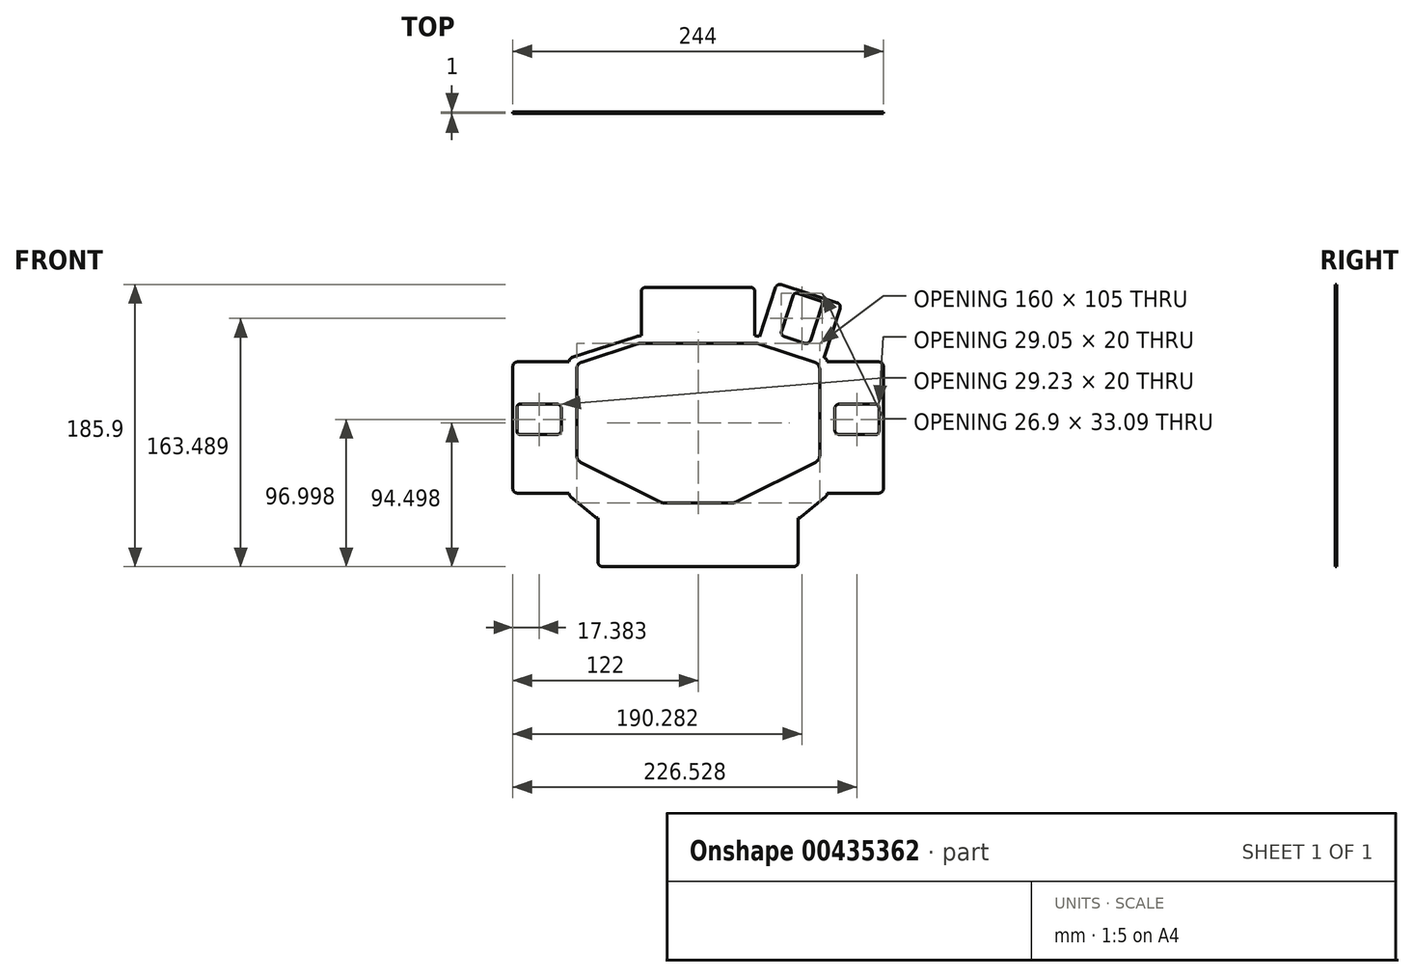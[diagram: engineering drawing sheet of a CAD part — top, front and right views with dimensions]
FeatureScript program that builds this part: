
annotation { "Feature Type Name" : "Feature", "Feature Type Description" : "" }
export const myFeature = defineFeature(function(context is Context, id is Id, definition is map)
    precondition{}
    {
        {
            var Q0;
            Q0=qCreatedBy(makeId("Front.planeOp"),FACE);
            var sketch = newSketch(context, id + "F0", { "sketchPlane" : qUnion([Q0])});
            skLineSegment(sketch, "E0", {"start": v(85, 6.93) * mm, "end": v(85, 93.35) * mm});
            skLineSegment(sketch, "E1", {"start": v(82.93, 96.2) * mm, "end": v(40.51, 110.04) * mm});
            skLineSegment(sketch, "E2", {"start": v(83.92, 4.63) * mm, "end": v(67.83, -8.78) * mm});
            skLineSegment(sketch, "E3", {"start": v(85, 95.53) * mm, "end": v(85, 25.53) * mm});
            skLineSegment(sketch, "E4", {"start": v(39.76, 105.28) * mm, "end": v(76.55, 93.28) * mm});
            skLineSegment(sketch, "E5", {"start": v(85, 90.53) * mm, "end": v(85, 95.53) * mm});
            skLineSegment(sketch, "E6", {"start": v(80, 88.53) * mm, "end": v(80, 31.7) * mm});
            skLineSegment(sketch, "E7", {"start": v(77.24, 27.24) * mm, "end": v(24.88, 1.06) * mm});
            skLineSegment(sketch, "E8", {"start": v(0, 0) * mm, "end": v(0, 0.53) * mm});
            skPoint(sketch, "E8.endSnap0", {"position": v(0, 0) * mm});
            skLineSegment(sketch, "E9", {"start": v(0, 0.53) * mm, "end": v(22.64, 0.53) * mm});
            skPoint(sketch, "E10.orphan", {"position": v(22.76, 0) * mm});
            skPoint(sketch, "E11.visualSharp", {"position": v(80, 92.16) * mm});
            skArc(sketch, "E11.filletArc", {"start": v(80, 88.53) * mm, "mid": v(79.05, 91.47) * mm, "end": v(76.55, 93.28) * mm});
            skPoint(sketch, "E12.visualSharp", {"position": v(80, 28.62) * mm});
            skArc(sketch, "E12.filletArc", {"start": v(77.24, 27.24) * mm, "mid": v(79.25, 29.08) * mm, "end": v(80, 31.7) * mm});
            skPoint(sketch, "E13.visualSharp", {"position": v(23.82, 0.53) * mm});
            skArc(sketch, "E13.filletArc", {"start": v(22.64, 0.53) * mm, "mid": v(23.79, 0.66) * mm, "end": v(24.88, 1.06) * mm});
            skPoint(sketch, "E14.visualSharp", {"position": v(39, 105.53) * mm});
            skArc(sketch, "E14.filletArc", {"start": v(39.76, 105.28) * mm, "mid": v(39, 105.47) * mm, "end": v(38.2, 105.53) * mm});
            skLineSegment(sketch, "E15", {"start": v(40.51, 110.04) * mm, "end": v(62, 103.03) * mm});
            skLineSegment(sketch, "E16", {"start": v(62, 103.03) * mm, "end": v(71.5, 99.93) * mm});
            skLineSegment(sketch, "E17", {"start": v(71.5, 99.93) * mm, "end": v(52.5, 106.13) * mm});
            skPoint(sketch, "E18.visualSharp", {"position": v(67, -9.47) * mm});
            skArc(sketch, "E18.filletArc", {"start": v(65.91, -9.47) * mm, "mid": v(66.94, -9.3) * mm, "end": v(67.83, -8.78) * mm});
            skPoint(sketch, "E19.visualSharp", {"position": v(85, 5.53) * mm});
            skArc(sketch, "E19.filletArc", {"start": v(83.92, 4.63) * mm, "mid": v(84.72, 5.66) * mm, "end": v(85, 6.93) * mm});
            skLineSegment(sketch, "E20", {"start": v(85, 95.53) * mm, "end": v(85, 65.53) * mm});
            skLineSegment(sketch, "E21", {"start": v(85, 65.53) * mm, "end": v(85, 45.53) * mm});
            skPoint(sketch, "E22.visualSharp", {"position": v(39, 110.53) * mm});
            skPoint(sketch, "E23.visualSharp", {"position": v(85, 95.53) * mm});
            skArc(sketch, "E23.filletArc", {"start": v(85, 93.35) * mm, "mid": v(84.43, 95.11) * mm, "end": v(82.93, 96.2) * mm});
            skLineSegment(sketch, "E24", {"start": v(85, 93.35) * mm, "end": v(114, 93.35) * mm});
            skLineSegment(sketch, "E25", {"start": v(85, 6.93) * mm, "end": v(114, 6.93) * mm});
            skPoint(sketch, "E26.visualSharp", {"position": v(117, 6.93) * mm});
            skPoint(sketch, "E27.newPointB", {"position": v(85, 45.53) * mm});
            skPoint(sketch, "E28.visualSharp", {"position": v(117, 93.35) * mm});
            skLineSegment(sketch, "E29", {"start": v(65.91, -9.47) * mm, "end": v(65.91, -38.47) * mm});
            skPoint(sketch, "E30.visualSharp", {"position": v(65.91, -41.47) * mm});
            skArc(sketch, "E30.filletArc", {"start": v(62.91, -41.47) * mm, "mid": v(65.04, -40.6) * mm, "end": v(65.91, -38.47) * mm});
            skArc(sketch, "E31.filletArc", {"start": v(40.51, 110.04) * mm, "mid": v(38.98, 110.4) * mm, "end": v(37.41, 110.53) * mm});
            skLineSegment(sketch, "E32", {"start": v(37.41, 110.53) * mm, "end": v(37.41, 139.53) * mm});
            skPoint(sketch, "E33.visualSharp", {"position": v(37.41, 142.53) * mm});
            skArc(sketch, "E33.filletArc", {"start": v(37.41, 139.53) * mm, "mid": v(36.53, 141.65) * mm, "end": v(34.41, 142.53) * mm});
            skLineSegment(sketch, "E34", {"start": v(39, 105.53) * mm, "end": v(38.2, 100.53) * mm});
            skLineSegment(sketch, "E35", {"start": v(80, 92.16) * mm, "end": v(75, 88.53) * mm});
            skLineSegment(sketch, "E36", {"start": v(80, 28.62) * mm, "end": v(75, 31.7) * mm});
            skLineSegment(sketch, "E37", {"start": v(23.82, 0.53) * mm, "end": v(22.64, 5.53) * mm});
            skLineSegment(sketch, "E38", {"start": v(114, 93.35) * mm, "end": v(117, 93.35) * mm});
            skLineSegment(sketch, "E39", {"start": v(117, 93.35) * mm, "end": v(119, 93.35) * mm});
            skLineSegment(sketch, "E40", {"start": v(122, 90.35) * mm, "end": v(122, 9.93) * mm});
            skLineSegment(sketch, "E41", {"start": v(119, 6.93) * mm, "end": v(117, 6.93) * mm});
            skLineSegment(sketch, "E42", {"start": v(114, 6.93) * mm, "end": v(117, 6.93) * mm});
            skPoint(sketch, "E43.visualSharp", {"position": v(122, 93.35) * mm});
            skArc(sketch, "E43.filletArc", {"start": v(122, 90.35) * mm, "mid": v(121.12, 92.47) * mm, "end": v(119, 93.35) * mm});
            skPoint(sketch, "E44.visualSharp", {"position": v(122, 6.93) * mm});
            skArc(sketch, "E44.filletArc", {"start": v(119, 6.93) * mm, "mid": v(121.12, 7.81) * mm, "end": v(122, 9.93) * mm});
            skLineSegment(sketch, "E45", {"start": v(80, 31.7) * mm, "end": v(75, 31.7) * mm});
            skLineSegment(sketch, "E46", {"start": v(80, 88.53) * mm, "end": v(75, 88.53) * mm});
            skLineSegment(sketch, "E47", {"start": v(62, 103.03) * mm, "end": v(63.55, 107.78) * mm});
            skLineSegment(sketch, "E48", {"start": v(54.97, 113.73) * mm, "end": v(61.8, 134.65) * mm});
            skLineSegment(sketch, "E49", {"start": v(80.8, 128.45) * mm, "end": v(73.99, 107.53) * mm});
            skPoint(sketch, "E50.visualSharp", {"position": v(62.72, 137.5) * mm});
            skPoint(sketch, "E51.visualSharp", {"position": v(81.74, 131.3) * mm});
            skLineSegment(sketch, "E52", {"start": v(63.55, 107.78) * mm, "end": v(73.06, 104.68) * mm});
            skLineSegment(sketch, "E53", {"start": v(70.2, 105.61) * mm, "end": v(56.9, 109.95) * mm});
            skLineSegment(sketch, "E54", {"start": v(82.93, 96.2) * mm, "end": v(93.47, 128.53) * mm});
            skLineSegment(sketch, "E55", {"start": v(40.51, 110.04) * mm, "end": v(51.05, 142.36) * mm});
            skLineSegment(sketch, "E56", {"start": v(54.83, 144.28) * mm, "end": v(91.55, 132.3) * mm});
            skPoint(sketch, "E57.visualSharp", {"position": v(94.4, 131.38) * mm});
            skArc(sketch, "E57.filletArc", {"start": v(93.47, 128.53) * mm, "mid": v(93.3, 130.82) * mm, "end": v(91.55, 132.3) * mm});
            skPoint(sketch, "E58.visualSharp", {"position": v(51.98, 145.21) * mm});
            skArc(sketch, "E58.filletArc", {"start": v(54.83, 144.28) * mm, "mid": v(52.54, 144.1) * mm, "end": v(51.05, 142.36) * mm});
            skLineSegment(sketch, "E59", {"start": v(34.41, 142.53) * mm, "end": v(0, 142.53) * mm});
            skLineSegment(sketch, "E60", {"start": v(62.91, -41.47) * mm, "end": v(0, -41.47) * mm});
            skPoint(sketch, "E61.orphan", {"position": v(0, 88.53) * mm});
            skLineSegment(sketch, "E62", {"start": v(38.2, 105.53) * mm, "end": v(0, 105.53) * mm});
            skArc(sketch, "E63.MirrorCS", {"start": v(-39.76, 105.28) * mm, "mid": v(-39, 105.47) * mm, "end": v(-38.2, 105.53) * mm});
            skArc(sketch, "E64.MirrorCS", {"start": v(-40.51, 110.04) * mm, "mid": v(-38.98, 110.4) * mm, "end": v(-37.41, 110.53) * mm});
            skArc(sketch, "E65.MirrorCS", {"start": v(-83.92, 4.63) * mm, "mid": v(-84.72, 5.66) * mm, "end": v(-85, 6.93) * mm});
            skLineSegment(sketch, "E66.MirrorCS", {"start": v(-39, 105.53) * mm, "end": v(-38.2, 100.53) * mm});
            skArc(sketch, "E67.MirrorCS", {"start": v(-85, 93.35) * mm, "mid": v(-84.43, 95.11) * mm, "end": v(-82.93, 96.2) * mm});
            skArc(sketch, "E68.MirrorCS", {"start": v(-22.64, 0.53) * mm, "mid": v(-23.79, 0.66) * mm, "end": v(-24.88, 1.06) * mm});
            skLineSegment(sketch, "E69.MirrorCS", {"start": v(-85, 90.53) * mm, "end": v(-85, 95.53) * mm});
            skLineSegment(sketch, "E70.MirrorCS", {"start": v(-23.82, 0.53) * mm, "end": v(-22.64, 5.53) * mm});
            skArc(sketch, "E71.MirrorCS", {"start": v(-77.24, 27.24) * mm, "mid": v(-79.25, 29.08) * mm, "end": v(-80, 31.7) * mm});
            skLineSegment(sketch, "E72.MirrorCS", {"start": v(-80, 28.62) * mm, "end": v(-75, 31.7) * mm});
            skLineSegment(sketch, "E73.MirrorCS", {"start": v(-80, 31.7) * mm, "end": v(-75, 31.7) * mm});
            skArc(sketch, "E74.MirrorCS", {"start": v(-80, 88.53) * mm, "mid": v(-79.05, 91.47) * mm, "end": v(-76.55, 93.28) * mm});
            skLineSegment(sketch, "E75.MirrorCS", {"start": v(-80, 92.16) * mm, "end": v(-75, 88.53) * mm});
            skArc(sketch, "E76.MirrorCS", {"start": v(-65.91, -9.47) * mm, "mid": v(-66.94, -9.3) * mm, "end": v(-67.83, -8.78) * mm});
            skLineSegment(sketch, "E77.MirrorCS", {"start": v(-80, 88.53) * mm, "end": v(-75, 88.53) * mm});
            skLineSegment(sketch, "E78.MirrorCS", {"start": v(-119, 6.93) * mm, "end": v(-117, 6.93) * mm});
            skArc(sketch, "E79.MirrorCS", {"start": v(-62.91, -41.47) * mm, "mid": v(-65.04, -40.6) * mm, "end": v(-65.91, -38.47) * mm});
            skLineSegment(sketch, "E80.MirrorCS", {"start": v(-114, 6.93) * mm, "end": v(-117, 6.93) * mm});
            skLineSegment(sketch, "E81.MirrorCS", {"start": v(-117, 93.35) * mm, "end": v(-119, 93.35) * mm});
            skLineSegment(sketch, "E82.MirrorCS", {"start": v(-62, 103.03) * mm, "end": v(-63.55, 107.78) * mm});
            skLineSegment(sketch, "E83.MirrorCS", {"start": v(-62, 103.03) * mm, "end": v(-71.5, 99.93) * mm});
            skLineSegment(sketch, "E84.MirrorCS", {"start": v(-114, 93.35) * mm, "end": v(-117, 93.35) * mm});
            skLineSegment(sketch, "E85.MirrorCS", {"start": v(-63.55, 107.78) * mm, "end": v(-73.06, 104.68) * mm});
            skLineSegment(sketch, "E86.MirrorCS", {"start": v(-40.51, 110.04) * mm, "end": v(-62, 103.03) * mm});
            skArc(sketch, "E87.MirrorCS", {"start": v(-122, 90.35) * mm, "mid": v(-121.12, 92.47) * mm, "end": v(-119, 93.35) * mm});
            skArc(sketch, "E88.MirrorCS", {"start": v(-54.83, 144.28) * mm, "mid": v(-52.54, 144.1) * mm, "end": v(-51.05, 142.36) * mm});
            skArc(sketch, "E89.MirrorCS", {"start": v(-93.47, 128.53) * mm, "mid": v(-93.3, 130.82) * mm, "end": v(-91.55, 132.3) * mm});
            skArc(sketch, "E90.MirrorCS", {"start": v(-119, 6.93) * mm, "mid": v(-121.12, 7.81) * mm, "end": v(-122, 9.93) * mm});
            skArc(sketch, "E91.MirrorCS", {"start": v(-90, 48.53) * mm, "mid": v(-90.88, 46.4) * mm, "end": v(-93, 45.53) * mm});
            skArc(sketch, "E92.MirrorCS", {"start": v(-37.41, 139.53) * mm, "mid": v(-36.53, 141.65) * mm, "end": v(-34.41, 142.53) * mm});
            skLineSegment(sketch, "E93.MirrorCS", {"start": v(-82.93, 96.2) * mm, "end": v(-40.51, 110.04) * mm});
            skLineSegment(sketch, "E94.MirrorCS", {"start": v(-85, 65.53) * mm, "end": v(-85, 45.53) * mm});
            skArc(sketch, "E95.MirrorCS", {"start": v(-93, 65.53) * mm, "mid": v(-90.88, 64.65) * mm, "end": v(-90, 62.53) * mm});
            skLineSegment(sketch, "E96.MirrorCS", {"start": v(-71.5, 99.93) * mm, "end": v(-52.5, 106.13) * mm});
            skLineSegment(sketch, "E97.MirrorCS", {"start": v(-90, 62.53) * mm, "end": v(-90, 48.53) * mm});
            skLineSegment(sketch, "E98.MirrorCS", {"start": v(-70.2, 105.61) * mm, "end": v(-56.9, 109.95) * mm});
            skPoint(sketch, "E99.MirrorP", {"position": v(-39, 110.53) * mm});
            skLineSegment(sketch, "E100.MirrorCS", {"start": v(-115, 65.53) * mm, "end": v(-93, 65.53) * mm});
            skLineSegment(sketch, "E101.MirrorCS", {"start": v(-65.91, -9.47) * mm, "end": v(-65.91, -38.47) * mm});
            skPoint(sketch, "E102.MirrorP", {"position": v(-39, 105.53) * mm});
            skLineSegment(sketch, "E103.MirrorCS", {"start": v(-90, 55.53) * mm, "end": v(-118, 55.53) * mm});
            skLineSegment(sketch, "E104.MirrorCS", {"start": v(-80.42, 127.25) * mm, "end": v(-73.99, 107.53) * mm});
            skLineSegment(sketch, "E105.MirrorCS", {"start": v(-85, 95.53) * mm, "end": v(-85, 65.53) * mm});
            skPoint(sketch, "E106.MirrorP", {"position": v(-22.76, 0) * mm});
            skLineSegment(sketch, "E107.MirrorCS", {"start": v(-54.83, 144.28) * mm, "end": v(-91.55, 132.3) * mm});
            skLineSegment(sketch, "E108.MirrorCS", {"start": v(-83.92, 4.63) * mm, "end": v(-67.83, -8.78) * mm});
            skLineSegment(sketch, "E109.MirrorCS", {"start": v(-85, 93.35) * mm, "end": v(-114, 93.35) * mm});
            skLineSegment(sketch, "E110.MirrorCS", {"start": v(-85, 6.93) * mm, "end": v(-85, 93.35) * mm});
            skPoint(sketch, "E111.MirrorP", {"position": v(-118, 45.53) * mm});
            skLineSegment(sketch, "E112.MirrorCS", {"start": v(-54.97, 113.73) * mm, "end": v(-61.8, 134.65) * mm});
            skLineSegment(sketch, "E113.MirrorCS", {"start": v(-80, 88.53) * mm, "end": v(-80, 31.7) * mm});
            skPoint(sketch, "E114.MirrorP", {"position": v(-94.4, 131.38) * mm});
            skLineSegment(sketch, "E115.MirrorCS", {"start": v(-122, 90.35) * mm, "end": v(-122, 9.93) * mm});
            skPoint(sketch, "E116.MirrorP", {"position": v(-117, 6.93) * mm});
            skPoint(sketch, "E117.MirrorP", {"position": v(-90, 65.53) * mm});
            skPoint(sketch, "E118.MirrorP", {"position": v(-90, 45.53) * mm});
            skLineSegment(sketch, "E119.MirrorCS", {"start": v(-85, 95.53) * mm, "end": v(-85, 25.53) * mm});
            skLineSegment(sketch, "E120.MirrorCS", {"start": v(-37.41, 110.53) * mm, "end": v(-37.41, 139.53) * mm});
            skPoint(sketch, "E121.MirrorP", {"position": v(-67, -9.47) * mm});
            skPoint(sketch, "E122.MirrorP", {"position": v(-122, 6.93) * mm});
            skPoint(sketch, "E123.MirrorP", {"position": v(-80, 28.62) * mm});
            skPoint(sketch, "E124.MirrorP", {"position": v(-85, 5.53) * mm});
            skLineSegment(sketch, "E125.MirrorCS", {"start": v(-40.51, 110.04) * mm, "end": v(-51.05, 142.36) * mm});
            skPoint(sketch, "E126.MirrorP", {"position": v(-65.91, -41.47) * mm});
            skLineSegment(sketch, "E127.MirrorCS", {"start": v(-82.93, 96.2) * mm, "end": v(-93.47, 128.53) * mm});
            skPoint(sketch, "E128.MirrorP", {"position": v(-118, 65.53) * mm});
            skLineSegment(sketch, "E129.MirrorCS", {"start": v(-85, 6.93) * mm, "end": v(-114, 6.93) * mm});
            skLineSegment(sketch, "E130.MirrorCS", {"start": v(-93, 45.53) * mm, "end": v(-115, 45.53) * mm});
            skLineSegment(sketch, "E131.MirrorCS", {"start": v(-39.76, 105.28) * mm, "end": v(-76.55, 93.28) * mm});
            skPoint(sketch, "E132.MirrorP", {"position": v(-117, 93.35) * mm});
            skLineSegment(sketch, "E133.MirrorCS", {"start": v(-38.2, 105.53) * mm, "end": v(0, 105.53) * mm});
            skLineSegment(sketch, "E134.MirrorCS", {"start": v(-62.91, -41.47) * mm, "end": v(0, -41.47) * mm});
            skLineSegment(sketch, "E135.MirrorCS", {"start": v(-34.41, 142.53) * mm, "end": v(0, 142.53) * mm});
            skPoint(sketch, "E136.MirrorP", {"position": v(-85, 95.53) * mm});
            skPoint(sketch, "E137.MirrorP", {"position": v(-85, 45.53) * mm});
            skPoint(sketch, "E138.MirrorP", {"position": v(-37.41, 142.53) * mm});
            skLineSegment(sketch, "E139.MirrorCS", {"start": v(-77.24, 27.24) * mm, "end": v(-24.88, 1.06) * mm});
            skPoint(sketch, "E140.MirrorP", {"position": v(-51.98, 145.21) * mm});
            skPoint(sketch, "E141.MirrorP", {"position": v(-23.82, 0.53) * mm});
            skPoint(sketch, "E142.MirrorP", {"position": v(-122, 93.35) * mm});
            skPoint(sketch, "E143.MirrorP", {"position": v(-80, 92.16) * mm});
            skLineSegment(sketch, "E144.MirrorCS", {"start": v(0, 0.53) * mm, "end": v(-22.64, 0.53) * mm});
            skPoint(sketch, "E145.newPointA", {"position": v(52.5, 106.13) * mm});
            skPoint(sketch, "E145.newPointB", {"position": v(54.04, 110.88) * mm});
            skArc(sketch, "E145.filletArc", {"start": v(54.97, 113.73) * mm, "mid": v(55.15, 111.44) * mm, "end": v(56.9, 109.95) * mm});
            skPoint(sketch, "E146.newPointA", {"position": v(71.5, 99.93) * mm});
            skPoint(sketch, "E146.newPointB", {"position": v(73.06, 104.68) * mm});
            skArc(sketch, "E146.filletArc", {"start": v(70.2, 105.61) * mm, "mid": v(72.5, 105.79) * mm, "end": v(73.99, 107.53) * mm});
            skPoint(sketch, "E147.newPointA", {"position": v(-71.5, 99.93) * mm});
            skPoint(sketch, "E147.newPointB", {"position": v(-73.06, 104.68) * mm});
            skArc(sketch, "E147.filletArc", {"start": v(-73.99, 107.53) * mm, "mid": v(-72.5, 105.79) * mm, "end": v(-70.2, 105.61) * mm});
            skPoint(sketch, "E148.newPointA", {"position": v(-54.04, 110.88) * mm});
            skPoint(sketch, "E148.newPointB", {"position": v(-52.5, 106.13) * mm});
            skArc(sketch, "E148.filletArc", {"start": v(-56.9, 109.95) * mm, "mid": v(-55.15, 111.44) * mm, "end": v(-54.97, 113.73) * mm});
            skLineSegment(sketch, "E149", {"start": v(-108.27, 45.53) * mm, "end": v(-116, 45.53) * mm});
            skLineSegment(sketch, "E150", {"start": v(-113.25, 65.53) * mm, "end": v(-116, 65.53) * mm});
            skLineSegment(sketch, "E151", {"start": v(-118, 47.53) * mm, "end": v(-118, 48.53) * mm});
            skPoint(sketch, "E152.end.orphan", {"position": v(-80.8, 128.45) * mm});
            skLineSegment(sketch, "E153", {"start": v(-73.06, 104.68) * mm, "end": v(-81.6, 130.86) * mm});
            skLineSegment(sketch, "E154", {"start": v(-80.31, 133.38) * mm, "end": v(-65.1, 138.34) * mm});
            skLineSegment(sketch, "E155", {"start": v(-61.8, 134.65) * mm, "end": v(-62.58, 137.06) * mm});
            skPoint(sketch, "E156.visualSharp", {"position": v(-82.21, 132.76) * mm});
            skArc(sketch, "E156.filletArc", {"start": v(-80.31, 133.38) * mm, "mid": v(-81.47, 132.38) * mm, "end": v(-81.6, 130.86) * mm});
            skArc(sketch, "E157.filletArc", {"start": v(-62.58, 137.06) * mm, "mid": v(-63.57, 138.22) * mm, "end": v(-65.1, 138.34) * mm});
            skPoint(sketch, "E158.start.orphan", {"position": v(78.89, 132.23) * mm});
            skLineSegment(sketch, "E159", {"start": v(54.04, 110.88) * mm, "end": v(62.62, 137.2) * mm});
            skLineSegment(sketch, "E160", {"start": v(65.14, 138.47) * mm, "end": v(80.36, 133.51) * mm});
            skLineSegment(sketch, "E161", {"start": v(80.8, 128.45) * mm, "end": v(81.64, 131) * mm});
            skPoint(sketch, "E162.visualSharp", {"position": v(63.24, 139.1) * mm});
            skArc(sketch, "E162.filletArc", {"start": v(65.14, 138.47) * mm, "mid": v(63.62, 138.36) * mm, "end": v(62.62, 137.2) * mm});
            skArc(sketch, "E163.filletArc", {"start": v(81.64, 131) * mm, "mid": v(81.52, 132.52) * mm, "end": v(80.36, 133.51) * mm});
            skLineSegment(sketch, "E164", {"start": v(-118, 55.53) * mm, "end": v(-119.23, 55.53) * mm});
            skLineSegment(sketch, "E165", {"start": v(-119.23, 55.53) * mm, "end": v(-119.23, 63.53) * mm});
            skLineSegment(sketch, "E166", {"start": v(-119.23, 55.53) * mm, "end": v(-119.23, 47.53) * mm});
            skLineSegment(sketch, "E167.trimOffspring", {"start": v(-118, 62.53) * mm, "end": v(-118, 63.53) * mm});
            skLineSegment(sketch, "E168", {"start": v(-113.25, 65.53) * mm, "end": v(-117.23, 65.53) * mm});
            skLineSegment(sketch, "E169", {"start": v(-115, 45.53) * mm, "end": v(-117.23, 45.53) * mm});
            skArc(sketch, "E170.filletArc", {"start": v(-117.23, 65.53) * mm, "mid": v(-118.65, 64.94) * mm, "end": v(-119.23, 63.53) * mm});
            skArc(sketch, "E171.filletArc", {"start": v(-119.23, 47.53) * mm, "mid": v(-118.65, 46.11) * mm, "end": v(-117.23, 45.53) * mm});
            skPoint(sketch, "E172.start.orphan", {"position": v(85, 55.53) * mm});
            skPoint(sketch, "E173.orphan", {"position": v(-85, 55.53) * mm});
            skLineSegment(sketch, "E174", {"start": v(85, 55.53) * mm, "end": v(90, 55.53) * mm});
            skLineSegment(sketch, "E175", {"start": v(90, 55.53) * mm, "end": v(119.05, 55.53) * mm});
            skLineSegment(sketch, "E176", {"start": v(119.05, 55.53) * mm, "end": v(119.05, 63.53) * mm});
            skLineSegment(sketch, "E177", {"start": v(117.05, 65.53) * mm, "end": v(93, 65.53) * mm});
            skLineSegment(sketch, "E178", {"start": v(90, 55.53) * mm, "end": v(90, 62.53) * mm});
            skLineSegment(sketch, "E179", {"start": v(119.05, 55.53) * mm, "end": v(119.05, 47.53) * mm});
            skLineSegment(sketch, "E180", {"start": v(117.05, 45.53) * mm, "end": v(93, 45.53) * mm});
            skLineSegment(sketch, "E181", {"start": v(90, 55.53) * mm, "end": v(90, 48.53) * mm});
            skPoint(sketch, "E182.newPointA", {"position": v(90, 65.53) * mm});
            skArc(sketch, "E182.filletArc", {"start": v(93, 65.53) * mm, "mid": v(90.88, 64.65) * mm, "end": v(90, 62.53) * mm});
            skArc(sketch, "E183.filletArc", {"start": v(90, 48.53) * mm, "mid": v(90.88, 46.4) * mm, "end": v(93, 45.53) * mm});
            skPoint(sketch, "E184.visualSharp", {"position": v(119.05, 65.53) * mm});
            skArc(sketch, "E184.filletArc", {"start": v(119.05, 63.53) * mm, "mid": v(118.47, 64.94) * mm, "end": v(117.05, 65.53) * mm});
            skPoint(sketch, "E185.visualSharp", {"position": v(119.05, 45.53) * mm});
            skArc(sketch, "E185.filletArc", {"start": v(117.05, 45.53) * mm, "mid": v(118.47, 46.11) * mm, "end": v(119.05, 47.53) * mm});
            skSolve(sketch);
        }
        {
            var Q0;
            Q0=makeQuery(id+"F0.imprint","IMPRINT",FACE,{"disambiguationData":[TD([[makeQuery(id+"F0.imprint","IMPRINT",EDGE,{"derivedFrom":sQuery(id+"F0.wireOp",EDGE,"E0")}),1.0]])]});
            var Q1;
            {var subQ12=sQuery(id+"F0.wireOp",EDGE,"E650.MirrorCS");Q1=makeQuery(id+"F0.imprint","IMPRINT",FACE,{"disambiguationData":[TD([[makeQuery(id+"F0.imprint","IMPRINT",EDGE,{"derivedFrom":subQ12}),1.0]])]});}
            var Q2;
            {var subQ6=sQuery(id+"F0.wireOp",EDGE,"E1");Q2=makeQuery(id+"F0.imprint","IMPRINT",FACE,{"disambiguationData":[TD([[makeQuery(id+"F0.imprint","IMPRINT",EDGE,{"derivedFrom":subQ6}),-1.0]])]});}
            var Q3;
            Q3=makeQuery(id+"F0.imprint","IMPRINT",FACE,{"disambiguationData":[TD([[makeQuery(id+"F0.imprint","IMPRINT",EDGE,{"derivedFrom":sQuery(id+"F0.wireOp",EDGE,"E0")}),-1.0]])]});
            var Q4;
            Q4=makeQuery(id+"F0.imprint","IMPRINT",FACE,{"disambiguationData":[TD([[makeQuery(id+"F0.imprint","IMPRINT",EDGE,{"derivedFrom":sQuery(id+"F0.wireOp",EDGE,"E78.MirrorCS")}),1.0]])]});
            var Q5;
            {var subQ0=sQuery(id+"F0.wireOp",EDGE,"E82.MirrorCS");Q5=makeQuery(id+"F0.imprint","IMPRINT",FACE,{"disambiguationData":[TD([[makeQuery(id+"F0.imprint","IMPRINT",EDGE,{"derivedFrom":subQ0}),1.0]])]});}
            var Q6;
            {var subQ0=sQuery(id+"F0.wireOp",EDGE,"E82.MirrorCS");Q6=makeQuery(id+"F0.imprint","IMPRINT",FACE,{"disambiguationData":[TD([[makeQuery(id+"F0.imprint","IMPRINT",EDGE,{"derivedFrom":subQ0}),-1.0]])]});}
            var Q7;
            {var subQ3=sQuery(id+"F0.wireOp",EDGE,"E47");Q7=makeQuery(id+"F0.imprint","IMPRINT",FACE,{"disambiguationData":[TD([[makeQuery(id+"F0.imprint","IMPRINT",EDGE,{"derivedFrom":subQ3}),1.0]])]});}
            var Q8;
            {var subQ3=sQuery(id+"F0.wireOp",EDGE,"E47");Q8=makeQuery(id+"F0.imprint","IMPRINT",FACE,{"disambiguationData":[TD([[makeQuery(id+"F0.imprint","IMPRINT",EDGE,{"derivedFrom":subQ3}),-1.0]])]});}
            var Q9;
            Q9=makeQuery(id+"F0.imprint","IMPRINT",FACE,{"disambiguationData":[TD([[makeQuery(id+"F0.imprint","IMPRINT",EDGE,{"derivedFrom":sQuery(id+"F0.wireOp",EDGE,"E88.MirrorCS")}),-1.0]])]});
            extrude(context, id + "F1", {"entities" : qUnion([Q0, Q1, Q2, Q3, Q4, Q5, Q6, Q7, Q8, Q9]), "depth" : 1 * mm, "offsetDistance" : 25 * mm});
        }
    });
